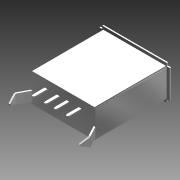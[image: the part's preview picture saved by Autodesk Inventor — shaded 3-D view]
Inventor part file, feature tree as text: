
AUTODESK INVENTOR PART (.ipt)
format: ipt  version: 2014 SP1 (Build 180222100, 222)  size: 186,880 bytes
history: native  units: in
note: dims shown in document units (in); Inventor stores cm internally (conversion verified against a paired STEP export)
features: mirror x1, imported_body x1
ambient origin geometry x8: Origin, YZ Plane, XZ Plane, XY Plane, X Axis, Y Axis, Z Axis, Center Point
bodies: Body1 (feature_tree)
feature tree (2):
  mirror  "Mirror2"
  imported_body  "Base1"
